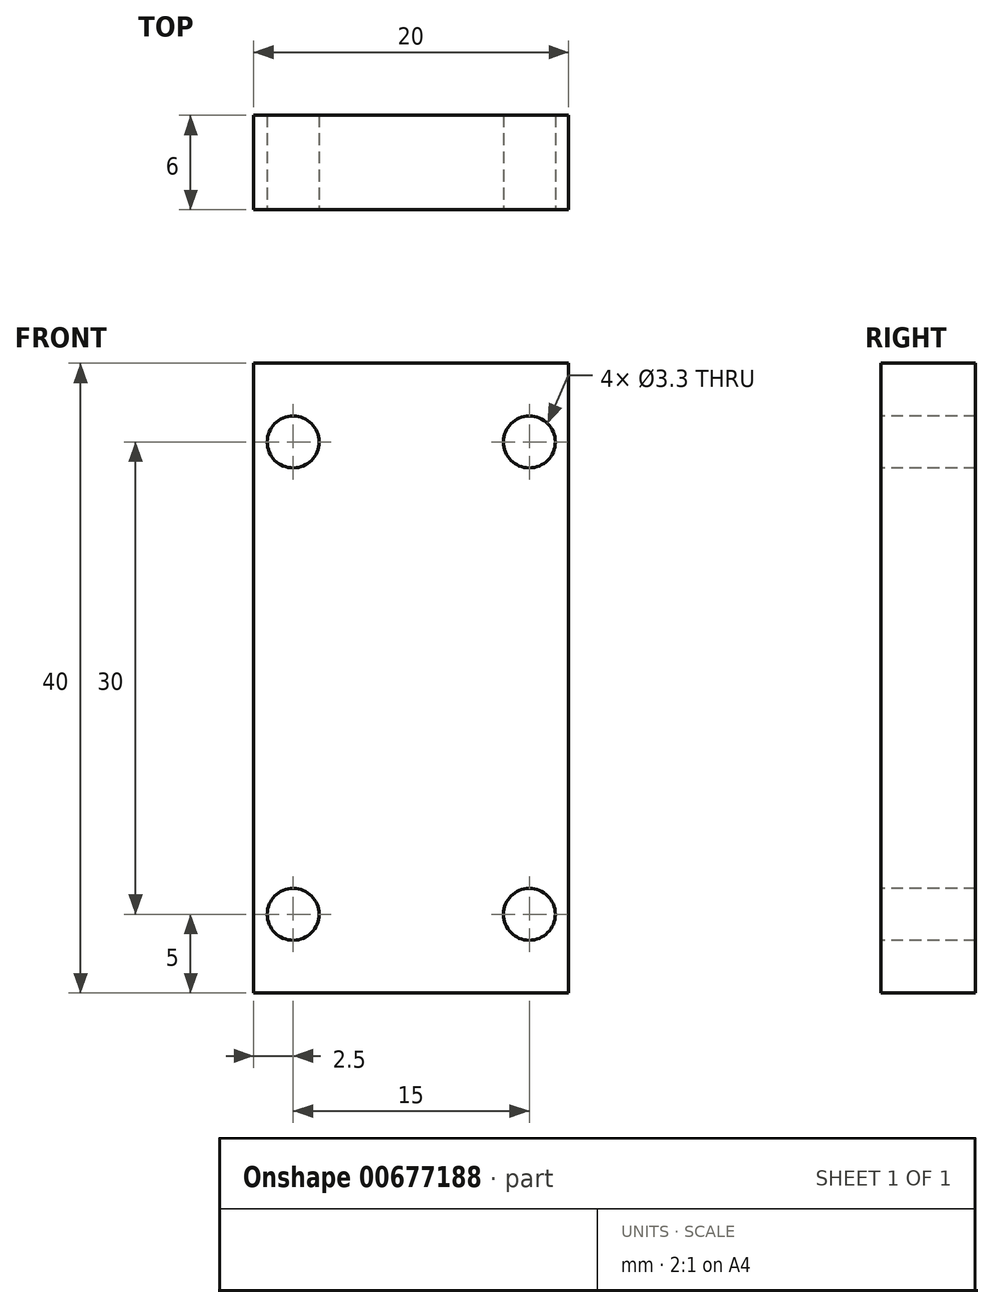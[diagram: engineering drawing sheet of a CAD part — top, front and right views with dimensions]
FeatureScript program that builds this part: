
annotation { "Feature Type Name" : "Feature", "Feature Type Description" : "" }
export const myFeature = defineFeature(function(context is Context, id is Id, definition is map)
    precondition{}
    {
        {
            var Q0;
            Q0=qCreatedBy(makeId("Front.planeOp"),FACE);
            var sketch = newSketch(context, id + "F0", { "sketchPlane" : qUnion([Q0])});
            skLineSegment(sketch, "E0.bottom", {"start": v(10, -20) * mm, "end": v(-10, -20) * mm});
            skLineSegment(sketch, "E0.top", {"start": v(10, 20) * mm, "end": v(-10, 20) * mm});
            skLineSegment(sketch, "E0.left", {"start": v(10, -20) * mm, "end": v(10, 20) * mm});
            skLineSegment(sketch, "E0.right", {"start": v(-10, -20) * mm, "end": v(-10, 20) * mm});
            skPoint(sketch, "E0.middle", {"position": v(0, 0) * mm});
            skSolve(sketch);
        }
        {
            var Q0;
            Q0 = qSketchRegion(id + "F0", true);
            extrude(context, id + "F1", {"entities" : qUnion([Q0]), "depth" : 6 * mm, "offsetDistance" : 25 * mm});
        }
        {
            var Q0;
            Q0=makeQuery(id+"F1.opExtrude","CAP_FACE",FACE,{"disambiguationData":[OSD([sQuery(id+"F0.wireOp",EDGE,"E0.bottom"),sQuery(id+"F0.wireOp",EDGE,"E0.top"),sQuery(id+"F0.wireOp",EDGE,"E0.left"),sQuery(id+"F0.wireOp",EDGE,"E0.right")])],"isStart":false});
            var sketch = newSketch(context, id + "F2", { "sketchPlane" : qUnion([Q0])});
            skPoint(sketch, "E1", {"position": v(7.5, 15) * mm});
            skPoint(sketch, "E2", {"position": v(-7.5, 15) * mm});
            skPoint(sketch, "E3", {"position": v(-7.5, -15) * mm});
            skPoint(sketch, "E4", {"position": v(7.5, -15) * mm});
            skSolve(sketch);
        }
        {
            var Q0;
            Q0=sQuery(id+"F2.wireOp",VERTEX,"E2");
            var Q1;
            Q1=sQuery(id+"F2.wireOp",VERTEX,"E1");
            var Q2;
            Q2=sQuery(id+"F2.wireOp",VERTEX,"E4");
            var Q3;
            Q3=sQuery(id+"F2.wireOp",VERTEX,"E3");
            var Q4;
            Q4=makeQuery(id+"F1.opExtrude","SWEPT_BODY",BODY,{"disambiguationData":[OSD([sQuery(id+"F0.wireOp",EDGE,"E0.bottom"),sQuery(id+"F0.wireOp",EDGE,"E0.top"),sQuery(id+"F0.wireOp",EDGE,"E0.left"),sQuery(id+"F0.wireOp",EDGE,"E0.right")])]});
            hole(context, id + "F3", {"style" : HoleStyle.SIMPLE, "endStyle" : HoleEndStyle.BLIND, "standardTappedOrClearance" : lookupTablePath({ "standard" : "ISO", "fit" : "Normal", "size" : "M3", "type" : "Clearance" }), "standardBlindInLast" : lookupTablePath({ "fit" : "Standard", "standard" : "ISO", "size" : "M3", "type" : "Clearance" }), "holeDiameter" : 3.3 * mm, "majorDiameter" : 5 * mm, "holeDepth" : 10 * mm, "isTappedThrough" : true, "tappedDepth" : 12 * mm, "tapClearance" : 3, "locations" : qUnion([Q0, Q1, Q2, Q3]), "scope" : qUnion([Q4])});
        }
    });
